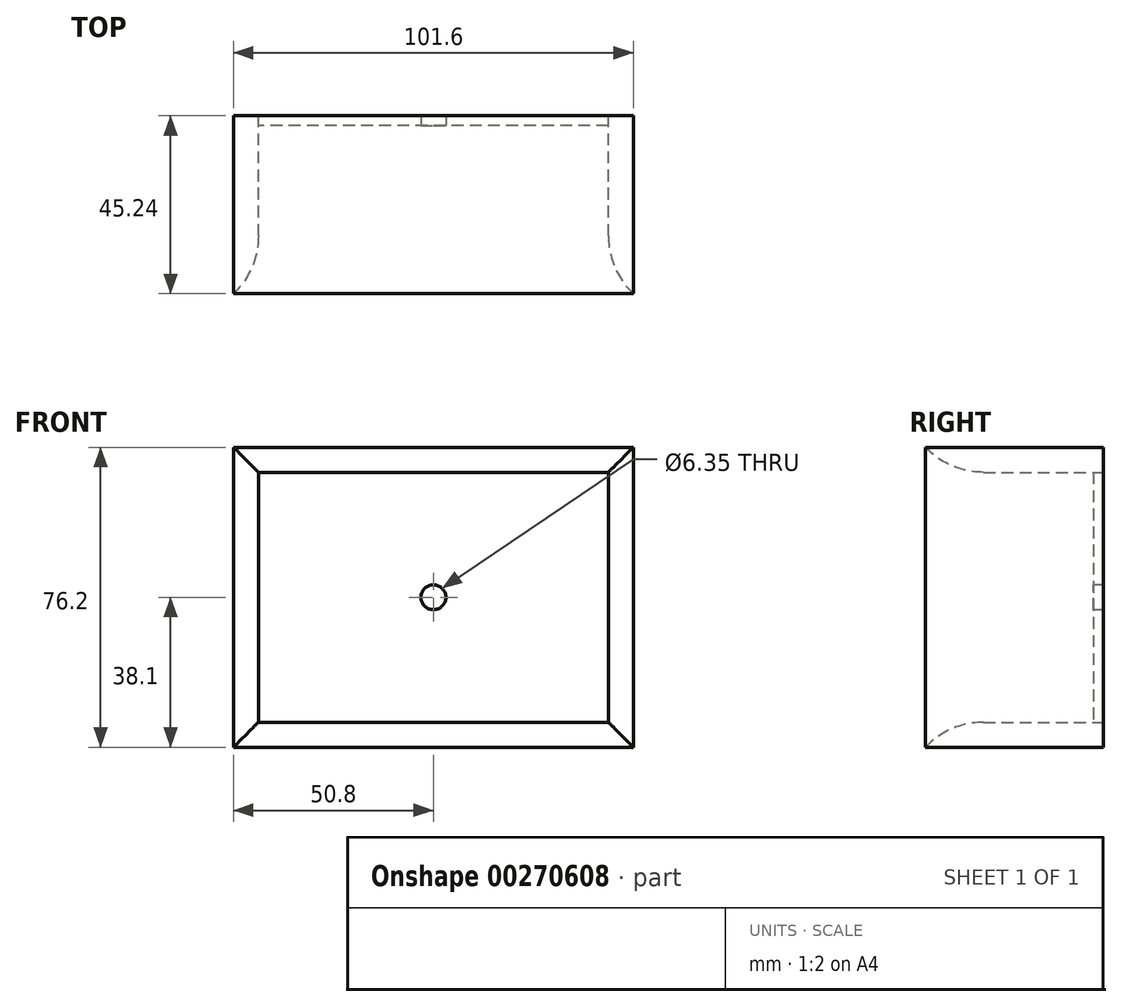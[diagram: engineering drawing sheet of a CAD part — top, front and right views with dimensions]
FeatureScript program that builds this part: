
annotation { "Feature Type Name" : "Feature", "Feature Type Description" : "" }
export const myFeature = defineFeature(function(context is Context, id is Id, definition is map)
    precondition{}
    {
        {
            var Q0;
            Q0=qCreatedBy(makeId("Front.planeOp"),FACE);
            var sketch = newSketch(context, id + "F0", { "sketchPlane" : qUnion([Q0])});
            skLineSegment(sketch, "E0.bottom", {"start": v(50.8, 38.1) * mm, "end": v(-50.8, 38.1) * mm});
            skLineSegment(sketch, "E0.top", {"start": v(50.8, -38.1) * mm, "end": v(-50.8, -38.1) * mm});
            skLineSegment(sketch, "E0.left", {"start": v(50.8, 38.1) * mm, "end": v(50.8, -38.1) * mm});
            skLineSegment(sketch, "E0.right", {"start": v(-50.8, 38.1) * mm, "end": v(-50.8, -38.1) * mm});
            skPoint(sketch, "E0.middle", {"position": v(0, 0) * mm});
            skLineSegment(sketch, "E1.bottom", {"start": v(44.45, 31.75) * mm, "end": v(-44.45, 31.75) * mm});
            skLineSegment(sketch, "E1.top", {"start": v(44.45, -31.75) * mm, "end": v(-44.45, -31.75) * mm});
            skLineSegment(sketch, "E1.left", {"start": v(44.45, 31.75) * mm, "end": v(44.45, -31.75) * mm});
            skLineSegment(sketch, "E1.right", {"start": v(-44.45, 31.75) * mm, "end": v(-44.45, -31.75) * mm});
            skSolve(sketch);
        }
        {
            var Q0;
            Q0=makeQuery(id+"F0.imprint","IMPRINT",FACE,{"disambiguationData":[TD([[makeQuery(id+"F0.imprint","IMPRINT",EDGE,{"derivedFrom":sQuery(id+"F0.wireOp",EDGE,"E0.bottom")}),1.0]])]});
            extrude(context, id + "F1", {"entities" : qUnion([Q0]), "depth" : 50.8 * mm});
        }
        {
            var Q0;
            Q0=makeQuery(id+"F0.imprint","IMPRINT",FACE,{"disambiguationData":[TD([[makeQuery(id+"F0.imprint","IMPRINT",EDGE,{"derivedFrom":sQuery(id+"F0.wireOp",EDGE,"E1.bottom")}),1.0]])]});
            extrude(context, id + "F2", {"entities" : qUnion([Q0]), "depth" : 2.54 * mm});
        }
        {
            var Q0;
            Q0=makeQuery(id+"F1.opExtrude","CAP_EDGE",EDGE,{"disambiguationData":[OSD([sQuery(id+"F0.wireOp",EDGE,"E1.right")])],"isStart":false});
            var Q1;
            Q1=makeQuery(id+"F1.opExtrude","CAP_EDGE",EDGE,{"disambiguationData":[OSD([sQuery(id+"F0.wireOp",EDGE,"E1.bottom")])],"isStart":false});
            var Q2;
            Q2=makeQuery(id+"F1.opExtrude","CAP_EDGE",EDGE,{"disambiguationData":[OSD([sQuery(id+"F0.wireOp",EDGE,"E1.left")])],"isStart":false});
            var Q3;
            Q3=makeQuery(id+"F1.opExtrude","CAP_EDGE",EDGE,{"disambiguationData":[OSD([sQuery(id+"F0.wireOp",EDGE,"E1.top")])],"isStart":false});
            fillet(context, id + "F3", {"entities" : qUnion([Q0, Q1, Q2, Q3]), "radius" : 20.32 * mm, "tangentPropagation" : true, "allowEdgeOverflow" : false});
        }
        {
            var Q0;
            Q0=makeQuery(id+"F2.opExtrude","CAP_FACE",FACE,{"disambiguationData":[OSD([sQuery(id+"F0.wireOp",EDGE,"E1.bottom"),sQuery(id+"F0.wireOp",EDGE,"E1.top"),sQuery(id+"F0.wireOp",EDGE,"E1.left"),sQuery(id+"F0.wireOp",EDGE,"E1.right")])],"isStart":false});
            var sketch = newSketch(context, id + "F4", { "sketchPlane" : qUnion([Q0])});
            skCircle(sketch, "E2", {"center": v(0, 0) * mm, "radius": 3.18 * mm});
            skSolve(sketch);
        }
        {
            var Q0;
            Q0=makeQuery(id+"F4.imprint","IMPRINT",FACE,{"disambiguationData":[TD([[makeQuery(id+"F4.imprint","IMPRINT",EDGE,{"derivedFrom":sQuery(id+"F4.wireOp",EDGE,"E2")}),1.0]])]});
            extrude(context, id + "F5", {"entities" : qUnion([Q0]), "operationType" : NewBodyOperationType.REMOVE, "endBound" : BoundingType.THROUGH_ALL, "oppositeDirection" : true, "depth" : 25.4 * mm});
        }
    });
